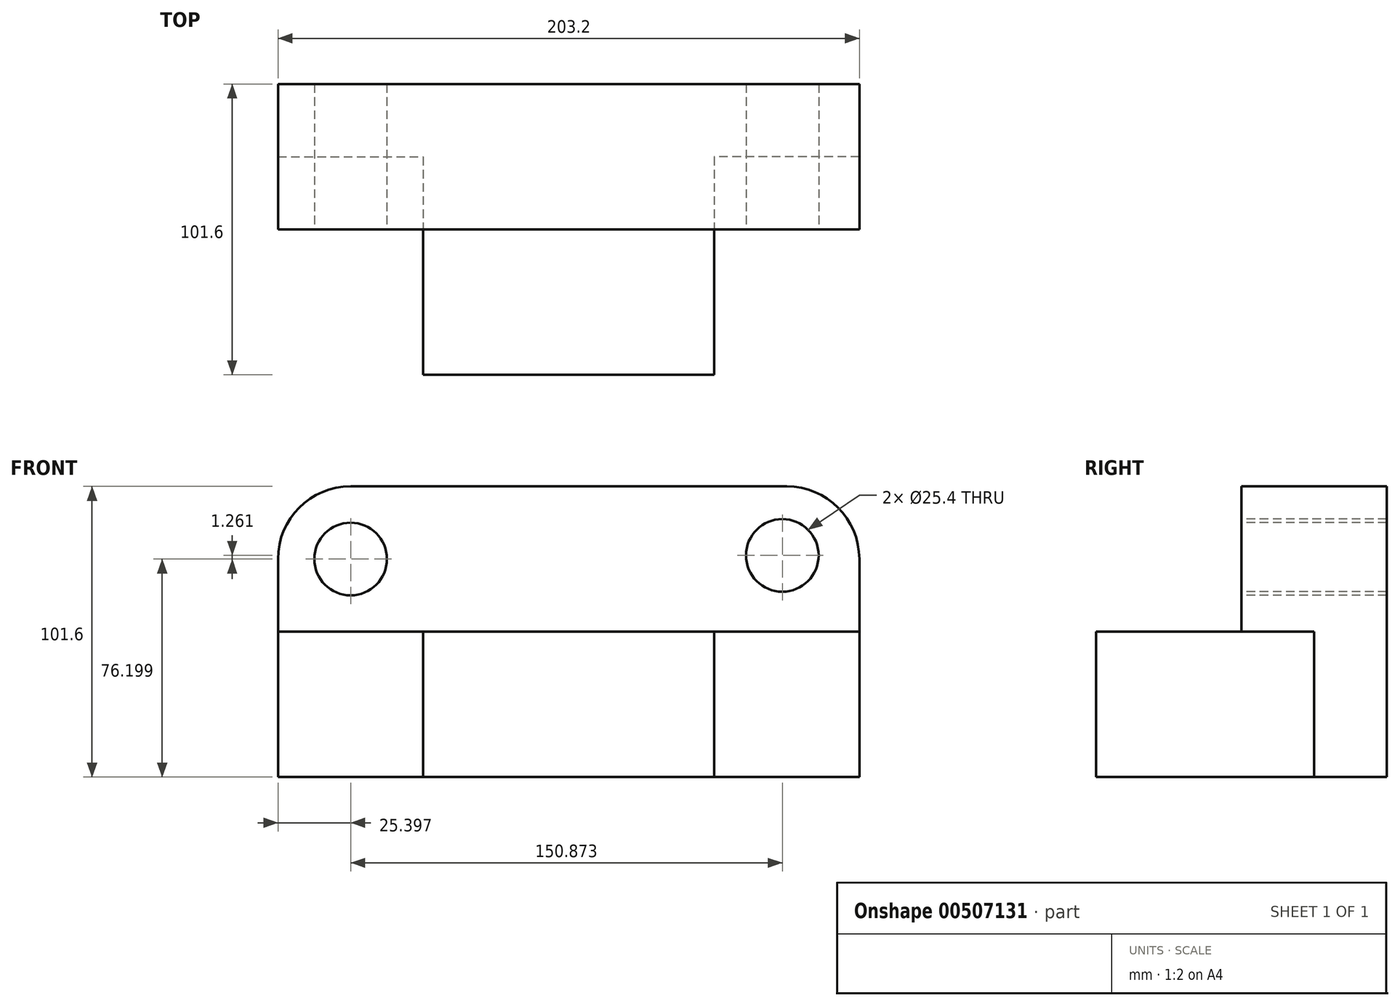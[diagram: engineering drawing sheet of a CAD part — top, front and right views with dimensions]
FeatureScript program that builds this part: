
annotation { "Feature Type Name" : "Feature", "Feature Type Description" : "" }
export const myFeature = defineFeature(function(context is Context, id is Id, definition is map)
    precondition{}
    {
        {
            var Q0;
            Q0=qCreatedBy(makeId("Front.planeOp"),FACE);
            var sketch = newSketch(context, id + "F0", { "sketchPlane" : qUnion([Q0])});
            skLineSegment(sketch, "E0.bottom", {"start": v(-108.18, 24.14) * mm, "end": v(95.02, 24.14) * mm});
            skLineSegment(sketch, "E0.top", {"start": v(-108.18, -77.46) * mm, "end": v(95.02, -77.46) * mm});
            skLineSegment(sketch, "E0.left", {"start": v(-108.18, 24.14) * mm, "end": v(-108.18, -77.46) * mm});
            skLineSegment(sketch, "E0.right", {"start": v(95.02, 24.14) * mm, "end": v(95.02, -77.46) * mm});
            skSolve(sketch);
        }
        {
            var Q0;
            Q0 = qSketchRegion(id + "F0", true);
            extrude(context, id + "F1", {"entities" : qUnion([Q0]), "oppositeDirection" : true, "depth" : 101.6 * mm, "offsetDistance" : 25.4 * mm});
        }
        {
            var Q0;
            Q0=qCreatedBy(makeId("Right.planeOp"),FACE);
            var sketch = newSketch(context, id + "F2", { "sketchPlane" : qUnion([Q0])});
            skLineSegment(sketch, "E1.bottom", {"start": v(0, 24.14) * mm, "end": v(50.8, 24.14) * mm});
            skLineSegment(sketch, "E1.top", {"start": v(0, -26.66) * mm, "end": v(50.8, -26.66) * mm});
            skLineSegment(sketch, "E1.left", {"start": v(0, 24.14) * mm, "end": v(0, -26.66) * mm});
            skLineSegment(sketch, "E1.right", {"start": v(50.8, 24.14) * mm, "end": v(50.8, -26.66) * mm});
            skSolve(sketch);
        }
        {
            var Q0;
            Q0 = qSketchRegion(id + "F2", true);
            extrude(context, id + "F3", {"entities" : qUnion([Q0]), "operationType" : NewBodyOperationType.REMOVE, "endBound" : BoundingType.SYMMETRIC, "oppositeDirection" : true, "depth" : 254 * mm, "offsetDistance" : 25.4 * mm});
        }
        {
            var Q0;
            Q0=qCreatedBy(makeId("Front.planeOp"),FACE);
            var sketch = newSketch(context, id + "F4", { "sketchPlane" : qUnion([Q0])});
            skLineSegment(sketch, "E2.bottom", {"start": v(-108.18, -26.66) * mm, "end": v(-57.38, -26.66) * mm});
            skLineSegment(sketch, "E2.top", {"start": v(-108.18, -77.46) * mm, "end": v(-57.38, -77.46) * mm});
            skLineSegment(sketch, "E2.left", {"start": v(-108.18, -26.66) * mm, "end": v(-108.18, -77.46) * mm});
            skLineSegment(sketch, "E2.right", {"start": v(-57.38, -26.66) * mm, "end": v(-57.38, -77.46) * mm});
            skSolve(sketch);
        }
        {
            var Q0;
            Q0 = qSketchRegion(id + "F4", true);
            extrude(context, id + "F5", {"entities" : qUnion([Q0]), "operationType" : NewBodyOperationType.REMOVE, "oppositeDirection" : true, "depth" : 76.2 * mm, "offsetDistance" : 25.4 * mm});
        }
        {
            var Q0;
            Q0=qCreatedBy(makeId("Front.planeOp"),FACE);
            var sketch = newSketch(context, id + "F6", { "sketchPlane" : qUnion([Q0])});
            skLineSegment(sketch, "E3.bottom", {"start": v(95.02, -77.46) * mm, "end": v(44.22, -77.46) * mm});
            skLineSegment(sketch, "E3.top", {"start": v(95.02, -26.66) * mm, "end": v(44.22, -26.66) * mm});
            skLineSegment(sketch, "E3.left", {"start": v(95.02, -77.46) * mm, "end": v(95.02, -26.66) * mm});
            skLineSegment(sketch, "E3.right", {"start": v(44.22, -77.46) * mm, "end": v(44.22, -26.66) * mm});
            skSolve(sketch);
        }
        {
            var Q0;
            Q0 = qSketchRegion(id + "F6", true);
            extrude(context, id + "F7", {"entities" : qUnion([Q0]), "operationType" : NewBodyOperationType.REMOVE, "oppositeDirection" : true, "depth" : 76.2 * mm, "offsetDistance" : 25.4 * mm});
        }
        {
            var Q0;
            Q0=makeQuery(id+"F1.opExtrude","SWEPT_EDGE",EDGE,{"disambiguationData":[OSD([sQuery(id+"F0.wireOp",EDGE,"E0.bottom"),sQuery(id+"F0.wireOp",EDGE,"E0.right")])]});
            fillet(context, id + "F8", {"entities" : qUnion([Q0]), "radius" : 25.4 * mm, "tangentPropagation" : true, "allowEdgeOverflow" : false});
        }
        {
            var Q0;
            Q0=makeQuery(id+"F1.opExtrude","SWEPT_EDGE",EDGE,{"disambiguationData":[OSD([sQuery(id+"F0.wireOp",EDGE,"E0.bottom"),sQuery(id+"F0.wireOp",EDGE,"E0.left")])]});
            fillet(context, id + "F9", {"entities" : qUnion([Q0]), "radius" : 25.4 * mm, "tangentPropagation" : true, "allowEdgeOverflow" : false});
        }
        {
            var Q0;
            Q0=qCreatedBy(makeId("Front.planeOp"),FACE);
            var sketch = newSketch(context, id + "F10", { "sketchPlane" : qUnion([Q0])});
            skCircle(sketch, "E4", {"center": v(-82.78, -1.26) * mm, "radius": 12.7 * mm});
            skSolve(sketch);
        }
        {
            var Q0;
            Q0=qCreatedBy(makeId("Front.planeOp"),FACE);
            var sketch = newSketch(context, id + "F11", { "sketchPlane" : qUnion([Q0])});
            skCircle(sketch, "E5", {"center": v(68.09, 0) * mm, "radius": 12.7 * mm});
            skSolve(sketch);
        }
        {
            var Q0;
            Q0 = qSketchRegion(id + "F11", true);
            extrude(context, id + "F12", {"entities" : qUnion([Q0]), "operationType" : NewBodyOperationType.REMOVE, "endBound" : BoundingType.THROUGH_ALL, "oppositeDirection" : true, "depth" : 25.4 * mm, "offsetDistance" : 25.4 * mm});
        }
        {
            var Q0;
            Q0 = qSketchRegion(id + "F10", true);
            extrude(context, id + "F13", {"entities" : qUnion([Q0]), "operationType" : NewBodyOperationType.REMOVE, "endBound" : BoundingType.THROUGH_ALL, "oppositeDirection" : true, "depth" : 25.4 * mm, "offsetDistance" : 25.4 * mm});
        }
    });
